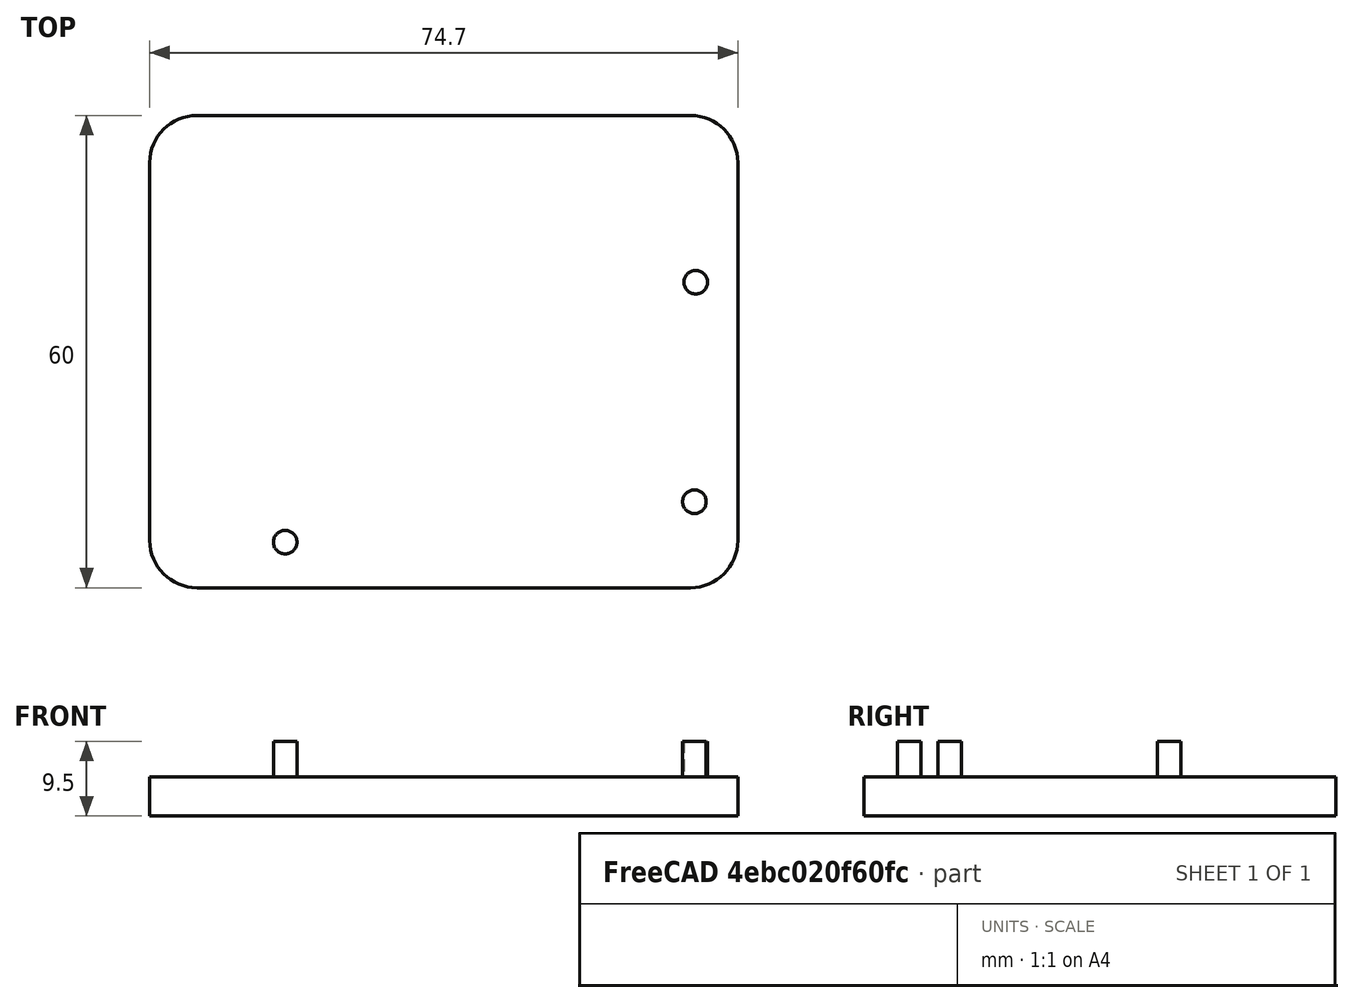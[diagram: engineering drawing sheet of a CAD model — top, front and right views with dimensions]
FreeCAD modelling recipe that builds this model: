
FCSTD DOCUMENT  (FreeCAD 1.0R38806 (Git))
Label: Soporte_placa
License: All rights reserved
LicenseURL: https://en.wikipedia.org/wiki/All_rights_reserved
objects: TechDraw::DrawViewDimension×5, TechDraw::DrawProjGroupItem×4, Sketcher::SketchObject×3, PartDesign::Pad×2, TechDraw::DrawProjGroup×2, PartDesign::Fillet×1, PartDesign::Body×1, TechDraw::DrawSVGTemplate×1, TechDraw::DrawPage×1
note: 21 computed .brp shape members not serialized (recipe doc carries the construction recipe); baked Part::Feature solids carry a one-line shape summary decoded from their .brp

FEATURE [Sketcher::SketchObject] Sketch  label="base"
  ArcFitTolerance = 1e-06
  AttachmentSupport = -> [XY_Plane]
  FullyConstrained = false
  MakeInternals = false
  MapMode = 5
  sketch-geometry (4):
    g0: LineSegment StartX=-37.5121 StartY=-29.9459 StartZ=0 EndX=37.1879 EndY=-29.9459 EndZ=0
    g1: LineSegment StartX=37.1879 StartY=-29.9459 StartZ=0 EndX=37.1879 EndY=30.0541 EndZ=0
    g2: LineSegment StartX=37.1879 StartY=30.0541 StartZ=0 EndX=-37.5121 EndY=30.0541 EndZ=0
    g3: LineSegment StartX=-37.5121 StartY=30.0541 StartZ=0 EndX=-37.5121 EndY=-29.9459 EndZ=0
  constraints (10):
    c: Coincident(g0,g1)
    c: Coincident(g1,g2)
    c: Coincident(g2,g3)
    c: Coincident(g3,g0)
    c: Horizontal(g0)
    c: Horizontal(g2)
    c: Vertical(g1)
    c: Vertical(g3)
    c: DistanceY(g3,g3) = 60
    c: DistanceX(g2,g2) = 74.7
FEATURE [PartDesign::Pad] Pad  label="extrusion_base"
  Direction = (0,0,1)
  Length = 5
  Length2 = 10
  Midplane = true
  Profile = -> Sketch
  ReferenceAxis = -> Sketch [N_Axis]
  Refine = true
  Suppressed = false
  Type = 0
  UseCustomVector = true
FEATURE [Sketcher::SketchObject] Sketch001
  ArcFitTolerance = 1e-06
  AttachmentSupport = -> [XY_Plane]
  FullyConstrained = false
  MakeInternals = false
  MapMode = 5
  sketch-geometry (3):
    g0: Circle CenterX=31.8445 CenterY=8.86758 CenterZ=0 NormalX=0 NormalY=0 NormalZ=1 AngleXU=0 Radius=1.5
    g1: Circle CenterX=31.6837 CenterY=-19.0134 CenterZ=0 NormalX=0 NormalY=0 NormalZ=1 AngleXU=0 Radius=1.5
    g2: Circle CenterX=-20.2977 CenterY=-24.1506 CenterZ=0 NormalX=0 NormalY=0 NormalZ=1 AngleXU=0 Radius=1.5
  constraints (3):
    c: Diameter(g0) = 3
    c: Diameter(g1) = 3
    c: Diameter(g2) = 3
FEATURE [PartDesign::Pad] Pad001  label="extrusion_barillas"
  BaseFeature = -> Pad
  Direction = (0,0,1)
  Length = 7
  Length2 = 10
  Profile = -> Sketch001
  ReferenceAxis = -> Sketch001 [N_Axis]
  Refine = true
  Suppressed = false
  Type = 0
FEATURE [PartDesign::Fillet] Fillet
  Base = -> Pad001 [Edge5,Edge1,Edge2,Edge8]
  BaseFeature = -> Pad001
  Radius = 6
  Refine = true
  SupportTransform = false
  Suppressed = false
  UseAllEdges = false
FEATURE [Sketcher::SketchObject] Sketch002  label="barillas"
  ArcFitTolerance = 1e-06
  AttachmentSupport = -> [XY_Plane]
  FullyConstrained = true
  MakeInternals = false
  MapMode = 5
FEATURE [PartDesign::Body] Body  label="placa_base"
  AllowCompound = false
  Group = -> [Sketch,Pad,Sketch001,Pad001,Fillet,Sketch002]
  Origin = -> Origin
  Tip = -> Fillet
FEATURE [TechDraw::DrawSVGTemplate] Template
  EditableTexts = approval_person=B. Hecate; creator=A. Nemesis; date_of_issue=12/14/24; document_status=In preparation; document_type=Assembly Drawing; drawing_number=DN; general_tolerances=ISO 2768-m; language_code=EN; part_material=Stainless steel Mat.No. 1.4301; responsible_department=RD; revision_index=AAA; sheet_number=1 / 1; sheet_scale=1 : 1; supplementary_title_1=ST1; supplementary_title_2=ST2; title=Soporte_placa
  Height = 297
  Orientation = 1
  Template = <path>
  Width = 420
FEATURE [TechDraw::DrawProjGroupItem] ProjItem  label="Front"
  CoarseView = false
  Direction = (0,-1,0)
  Focus = 100
  HardHidden = false
  IsoCount = 0
  IsoHidden = false
  IsoVisible = false
  LockPosition = true
  Perspective = false
  Rotation = 0
  RotationVector = (1,0,0)
  Scale = 2
  ScaleType = 0
  ScrubCount = 1
  SeamHidden = false
  SeamVisible = false
  SmoothHidden = false
  SmoothVisible = true
  Source = -> [Body]
  Type = 0
  X = 0
  XDirection = (1,0,0)
  Y = 0
FEATURE [TechDraw::DrawProjGroupItem] ProjItem001  label="Top"
  CoarseView = false
  Direction = (0,0,1)
  Focus = 100
  HardHidden = false
  IsoCount = 0
  IsoHidden = false
  IsoVisible = false
  LockPosition = false
  Perspective = false
  Rotation = 0
  RotationVector = (1,0,0)
  Scale = 2
  ScaleType = 0
  ScrubCount = 1
  SeamHidden = false
  SeamVisible = false
  SmoothHidden = false
  SmoothVisible = true
  Source = -> [Body]
  Type = 4
  X = 0
  XDirection = (1,0,0)
  Y = -84.5
FEATURE [TechDraw::DrawProjGroupItem] ProjItem002  label="Left"
  CoarseView = false
  Direction = (-1,-1e-16,0)
  Focus = 100
  HardHidden = false
  IsoCount = 0
  IsoHidden = false
  IsoVisible = false
  LockPosition = false
  Perspective = false
  Rotation = 0
  RotationVector = (1,0,0)
  Scale = 2
  ScaleType = 0
  ScrubCount = 1
  SeamHidden = false
  SeamVisible = false
  SmoothHidden = false
  SmoothVisible = true
  Source = -> [Body]
  Type = 1
  X = 149.7
  XDirection = (1e-16,-1,0)
  Y = 0
FEATURE [TechDraw::DrawProjGroup] ProjGroup
  Anchor = -> ProjItem
  AutoDistribute = true
  LockPosition = false
  ProjectionType = 0
  Rotation = 0
  Scale = 2
  ScaleType = 2
  Source = -> [Body]
  Views = -> [ProjItem,ProjItem001,ProjItem002]
  X = 124.911
  Y = 243.865
  spacingX = 15
  spacingY = 15
FEATURE [TechDraw::DrawProjGroupItem] ProjItem003  label="Front001"
  CoarseView = false
  Direction = (-0.523719,-0.733606,0.433059)
  Focus = 100
  HardHidden = false
  IsoCount = 0
  IsoHidden = false
  IsoVisible = false
  LockPosition = true
  Perspective = false
  Rotation = 0
  RotationVector = (0.812305,-0.583205,-0.00559643)
  Scale = 2
  ScaleType = 0
  ScrubCount = 1
  SeamHidden = false
  SeamVisible = false
  SmoothHidden = false
  SmoothVisible = true
  Source = -> [Body]
  Type = 0
  X = 0
  XDirection = (0.812305,-0.583205,-0.00559643)
  Y = 0
FEATURE [TechDraw::DrawProjGroup] ProjGroup001
  Anchor = -> ProjItem003
  AutoDistribute = true
  LockPosition = false
  ProjectionType = 0
  Rotation = 0
  Scale = 2
  ScaleType = 2
  Source = -> [Body]
  Views = -> [ProjItem003]
  X = 302.077
  Y = 142.745
  spacingX = 15
  spacingY = 15
FEATURE [TechDraw::DrawViewDimension] Dimension
  AngleOverride = false
  Arbitrary = false
  ArbitraryTolerances = false
  BoxCorners = (2) [(-74.7,-60,0),(74.7,60,0)]
  EqualTolerance = true
  ExtensionAngle = 0
  FormatSpec = %.2w
  FormatSpecOverTolerance = %+.2w
  FormatSpecUnderTolerance = %+.2w
  Inverted = false
  LineAngle = 0
  LockPosition = false
  MeasureType = 1
  OverTolerance = 0
  References2D = -> [ProjItem001]
  Rotation = 0
  ScaleType = 0
  TheoreticalExact = false
  Type = 1
  UnderTolerance = 0
  X = 0
  Y = -88.8021
FEATURE [TechDraw::DrawViewDimension] Dimension001
  AngleOverride = false
  Arbitrary = false
  ArbitraryTolerances = false
  BoxCorners = (2) [(-74.7,-60,0),(74.7,60,0)]
  EqualTolerance = true
  ExtensionAngle = 0
  FormatSpec = R%.2w
  FormatSpecOverTolerance = %+.2w
  FormatSpecUnderTolerance = %+.2w
  Inverted = false
  LineAngle = 0
  LockPosition = false
  MeasureType = 1
  OverTolerance = 0
  References2D = -> [ProjItem001]
  Rotation = 0
  ScaleType = 0
  TheoreticalExact = false
  Type = 4
  UnderTolerance = 0
  X = -84.7929
  Y = -63.3166
FEATURE [TechDraw::DrawViewDimension] Dimension002
  AngleOverride = false
  Arbitrary = false
  ArbitraryTolerances = false
  BoxCorners = (2) [(-74.7,-60,0),(74.7,60,0)]
  EqualTolerance = true
  ExtensionAngle = 0
  FormatSpec = ⌀%.2w
  FormatSpecOverTolerance = %+.2w
  FormatSpecUnderTolerance = %+.2w
  Inverted = false
  LineAngle = 0
  LockPosition = false
  MeasureType = 1
  OverTolerance = 0
  References2D = -> [ProjItem001]
  Rotation = 0
  ScaleType = 0
  TheoreticalExact = false
  Type = 5
  UnderTolerance = 0
  X = -28.1766
  Y = -38.6251
FEATURE [TechDraw::DrawViewDimension] Dimension003
  AngleOverride = false
  Arbitrary = false
  ArbitraryTolerances = false
  BoxCorners = (2) [(-74.7,-60,0),(74.7,60,0)]
  EqualTolerance = true
  ExtensionAngle = 0
  FormatSpec = %.2w
  FormatSpecOverTolerance = %+.2w
  FormatSpecUnderTolerance = %+.2w
  Inverted = false
  LineAngle = 0
  LockPosition = false
  MeasureType = 1
  OverTolerance = 0
  References2D = -> [ProjItem001]
  Rotation = 0
  ScaleType = 0
  TheoreticalExact = false
  Type = 2
  UnderTolerance = 0
  X = -89.4138
  Y = 0
FEATURE [TechDraw::DrawViewDimension] Dimension004
  AngleOverride = false
  Arbitrary = false
  ArbitraryTolerances = false
  BoxCorners = (2) [(-60,-9.5,-1e-07),(60,9.5,1e-07)]
  EqualTolerance = true
  ExtensionAngle = 0
  FormatSpec = %.2w
  FormatSpecOverTolerance = %+.2w
  FormatSpecUnderTolerance = %+.2w
  Inverted = false
  LineAngle = 0
  LockPosition = false
  MeasureType = 1
  OverTolerance = 0
  References2D = -> [ProjItem002]
  Rotation = 0
  ScaleType = 0
  TheoreticalExact = false
  Type = 0
  UnderTolerance = 0
  X = 74.7965
  Y = -22.8554
FEATURE [TechDraw::DrawPage] Page
  KeepUpdated = true
  NextBalloonIndex = 1
  ProjectionType = 0
  Template = -> Template
  Views = -> [ProjGroup,ProjGroup001,Dimension,Dimension001,Dimension002,Dimension003,Dimension004]
note: 1 file-system path scrubbed to <path> (originals preserved in the JSON sidecar)
